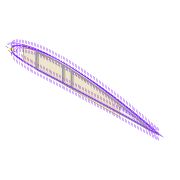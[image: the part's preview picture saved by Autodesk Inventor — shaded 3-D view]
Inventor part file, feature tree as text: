
AUTODESK INVENTOR PART (.ipt)
format: ipt  version: 2022 (Build 260153000, 153)  size: 361,984 bytes
history: native  units: mm
features: extrude x7, sketch x7, projected_geometry x5, shell x1, fillet x1, plane x1
ambient origin geometry x8: Origin, YZ Plane, XZ Plane, XY Plane, X Axis, Y Axis, Z Axis, Center Point
bodies: Solid1 (feature_tree)
feature tree (22):
  extrude  "Extrusion1"  Depth=5.0mm
  shell  "Shell1"  Thickness=2.0mm
  extrude  "Extrusion8"  Depth=5.9mm
  extrude  "Extrusion3"  Depth=10.0mm TaperAngle=0.0deg
  extrude  "Extrusion4"  Depth=2.0mm
  fillet  "Fillet1"  Radius=5.0mm
  extrude  "Extrusion5"  Depth=2.5mm
  plane  "Work Plane2"
  extrude  "Extrusion9"  Depth=1.6mm
  extrude  "Extrusion10"  Depth=0.5mm
  sketch  "Sketch3"  dims[d0=4.0mm d1=0.0mm d2=5.0mm d7=2.0mm]
  sketch  "Sketch8"  dims[d8=2.0mm d9=5.9mm]
  sketch  "Sketch9"  dims[d13=10.0mm d14=0.0mm d16=10.0mm d17=0.0mm]
  sketch  "Sketch10"  dims[d22=4.0mm d23=0.0mm d31=2.0mm d32=5.0mm]
  projected_geometry  "Projected Loop4"
  projected_geometry  "Projected Loop10"
  sketch  "Sketch24"  dims[d34=1.6mm d35=2.5mm]
  projected_geometry  "Projected Loop11"
  projected_geometry  "Projected Loop12"
  sketch  "Sketch26"  dims[d37=5.0mm d38=1.6mm]
  projected_geometry  "Projected Loop13"
  sketch  "Sketch27"  dims[d40=2.5mm d62=75.0mm d63=6.0mm d64=4.0mm d65=0.0mm d66=3.0mm d67=12.0mm d68=75.0mm d69=20.0mm d70=0.5mm d71=10.0mm d72=0.0mm d73=10.0mm d74=0.0mm]
